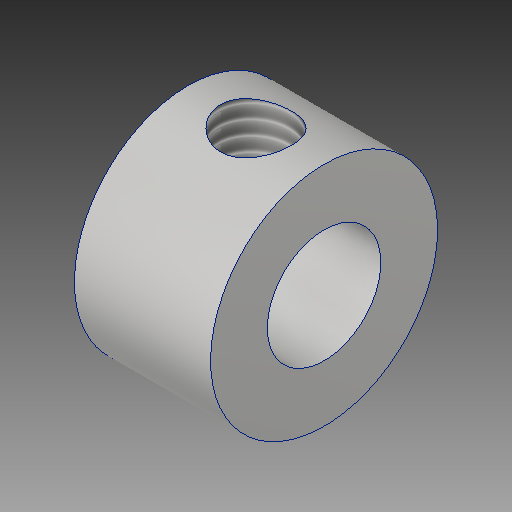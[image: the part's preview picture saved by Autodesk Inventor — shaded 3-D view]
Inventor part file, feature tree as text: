
AUTODESK INVENTOR PART (.ipt)
format: ipt  version: 2019 (Build 230136000, 136)  size: 134,144 bytes
history: native  units: in
note: dims shown in document units (in); Inventor stores cm internally (conversion verified against a paired STEP export)
features: other x3, sketch x2, plane x1
ambient origin geometry x8: Origin, YZ Plane, XZ Plane, XY Plane, X Axis, Y Axis, Z Axis, Center Point
bodies: Solid1 (feature_tree)
feature tree (6):
  other  "Collar.ipt"
  other  "Solid2::Collar.ipt"
  other  "TaggingFeature1"
  sketch  "Sketch2"  dims[d0=0.3937in]
  sketch  "Sketch3"
  plane  "Work Plane1"
